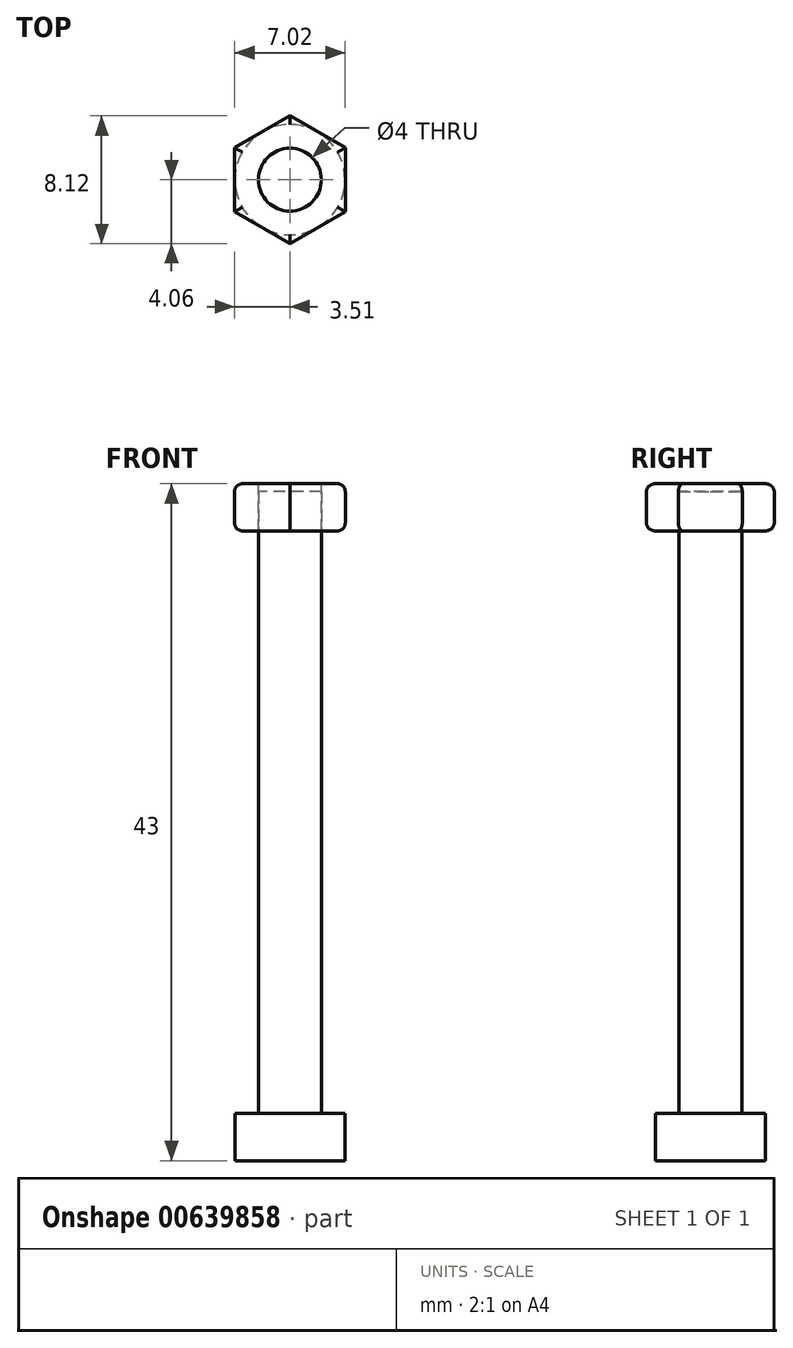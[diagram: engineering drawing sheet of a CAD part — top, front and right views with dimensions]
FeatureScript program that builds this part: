
annotation { "Feature Type Name" : "Feature", "Feature Type Description" : "" }
export const myFeature = defineFeature(function(context is Context, id is Id, definition is map)
    precondition{}
    {
        {
            var Q0;
            Q0=qCreatedBy(makeId("Top.planeOp"),FACE);
            var sketch = newSketch(context, id + "F0", { "sketchPlane" : qUnion([Q0])});
            skCircle(sketch, "E0", {"center": v(0, 0) * mm, "radius": 2 * mm});
            skCircle(sketch, "E1", {"center": v(0, 0) * mm, "radius": 3.5 * mm});
            skSolve(sketch);
        }
        {
            var Q0;
            Q0=makeQuery(id+"F0.imprint","IMPRINT",FACE,{"disambiguationData":[TD([[makeQuery(id+"F0.imprint","IMPRINT",EDGE,{"derivedFrom":sQuery(id+"F0.wireOp",EDGE,"E0")}),1.0]])]});
            extrude(context, id + "F1", {"entities" : qUnion([Q0]), "depth" : 40 * mm, "offsetDistance" : 25 * mm});
        }
        {
            var Q0;
            Q0=makeQuery(id+"F0.imprint","IMPRINT",FACE,{"disambiguationData":[TD([[makeQuery(id+"F0.imprint","IMPRINT",EDGE,{"derivedFrom":sQuery(id+"F0.wireOp",EDGE,"E0")}),-1.0]])]});
            var Q1;
            Q1=makeQuery(id+"F0.imprint","IMPRINT",FACE,{"disambiguationData":[TD([[makeQuery(id+"F0.imprint","IMPRINT",EDGE,{"derivedFrom":sQuery(id+"F0.wireOp",EDGE,"E0")}),1.0]])]});
            extrude(context, id + "F2", {"entities" : qUnion([Q0, Q1]), "operationType" : NewBodyOperationType.ADD, "oppositeDirection" : true, "depth" : 3 * mm, "offsetDistance" : 25 * mm});
        }
        {
            var Q0;
            Q0=makeQuery(id+"F1.opExtrude","CAP_FACE",FACE,{"disambiguationData":[OSD([sQuery(id+"F0.wireOp",EDGE,"E0")])],"isStart":false});
            var sketch = newSketch(context, id + "F3", { "sketchPlane" : qUnion([Q0])});
            skCircle(sketch, "E2.cCircle", {"center": v(0, 0) * mm, "radius": 3.51 * mm, "construction": true});
            skLineSegment(sketch, "E2.0", {"start": v(3.51, 2.03) * mm, "end": v(3.51, -2.03) * mm});
            skLineSegment(sketch, "E2.1", {"start": v(3.51, -2.03) * mm, "end": v(0, -4.06) * mm});
            skLineSegment(sketch, "E2.2", {"start": v(0, -4.06) * mm, "end": v(-3.51, -2.03) * mm});
            skLineSegment(sketch, "E2.3", {"start": v(-3.51, -2.03) * mm, "end": v(-3.51, 2.03) * mm});
            skLineSegment(sketch, "E2.4", {"start": v(-3.51, 2.03) * mm, "end": v(0, 4.06) * mm});
            skLineSegment(sketch, "E2.5", {"start": v(0, 4.06) * mm, "end": v(3.51, 2.03) * mm});
            skPoint(sketch, "E2.0.midPoint", {"position": v(3.51, 0) * mm});
            skCircle(sketch, "E3.0", {"center": v(0, 0) * mm, "radius": 2 * mm});
            skSolve(sketch);
        }
        {
            var Q0;
            Q0=makeQuery(id+"F3.imprint","IMPRINT",FACE,{"disambiguationData":[TD([[makeQuery(id+"F3.imprint","IMPRINT",EDGE,{"derivedFrom":sQuery(id+"F3.wireOp",EDGE,"E2.0")}),-1.0]])]});
            extrude(context, id + "F4", {"entities" : qUnion([Q0]), "oppositeDirection" : true, "depth" : 3 * mm, "offsetDistance" : 25 * mm});
        }
        {
            var Q0;
            Q0=makeQuery(id+"F3.imprint","IMPRINT",FACE,{"disambiguationData":[TD([[makeQuery(id+"F3.imprint","IMPRINT",EDGE,{"derivedFrom":sQuery(id+"F3.wireOp",EDGE,"E3.0")}),1.0]])]});
            extrude(context, id + "F5", {"entities" : qUnion([Q0]), "operationType" : NewBodyOperationType.REMOVE, "oppositeDirection" : true, "depth" : .5 * mm, "offsetDistance" : 25 * mm});
        }
        {
            var Q0;
            Q0=makeQuery(id+"F4.opExtrude","CAP_EDGE",EDGE,{"disambiguationData":[OSD([sQuery(id+"F3.wireOp",EDGE,"E2.0")])],"isStart":true});
            var Q1;
            Q1=makeQuery(id+"F4.opExtrude","CAP_EDGE",EDGE,{"disambiguationData":[OSD([sQuery(id+"F3.wireOp",EDGE,"E2.5")])],"isStart":true});
            var Q2;
            Q2=makeQuery(id+"F4.opExtrude","CAP_EDGE",EDGE,{"disambiguationData":[OSD([sQuery(id+"F3.wireOp",EDGE,"E2.4")])],"isStart":true});
            var Q3;
            Q3=makeQuery(id+"F4.opExtrude","CAP_EDGE",EDGE,{"disambiguationData":[OSD([sQuery(id+"F3.wireOp",EDGE,"E2.3")])],"isStart":true});
            var Q4;
            Q4=makeQuery(id+"F4.opExtrude","CAP_EDGE",EDGE,{"disambiguationData":[OSD([sQuery(id+"F3.wireOp",EDGE,"E2.2")])],"isStart":true});
            var Q5;
            Q5=makeQuery(id+"F4.opExtrude","CAP_EDGE",EDGE,{"disambiguationData":[OSD([sQuery(id+"F3.wireOp",EDGE,"E2.1")])],"isStart":true});
            var Q6;
            Q6=makeQuery(id+"F4.opExtrude","CAP_EDGE",EDGE,{"disambiguationData":[OSD([sQuery(id+"F3.wireOp",EDGE,"E2.1")])],"isStart":false});
            var Q7;
            Q7=makeQuery(id+"F4.opExtrude","CAP_EDGE",EDGE,{"disambiguationData":[OSD([sQuery(id+"F3.wireOp",EDGE,"E2.2")])],"isStart":false});
            var Q8;
            Q8=makeQuery(id+"F4.opExtrude","CAP_EDGE",EDGE,{"disambiguationData":[OSD([sQuery(id+"F3.wireOp",EDGE,"E2.3")])],"isStart":false});
            var Q9;
            Q9=makeQuery(id+"F4.opExtrude","CAP_EDGE",EDGE,{"disambiguationData":[OSD([sQuery(id+"F3.wireOp",EDGE,"E2.4")])],"isStart":false});
            var Q10;
            Q10=makeQuery(id+"F4.opExtrude","CAP_EDGE",EDGE,{"disambiguationData":[OSD([sQuery(id+"F3.wireOp",EDGE,"E2.5")])],"isStart":false});
            var Q11;
            Q11=makeQuery(id+"F4.opExtrude","CAP_EDGE",EDGE,{"disambiguationData":[OSD([sQuery(id+"F3.wireOp",EDGE,"E2.0")])],"isStart":false});
            fillet(context, id + "F6", {"entities" : qUnion([Q0, Q1, Q2, Q3, Q4, Q5, Q6, Q7, Q8, Q9, Q10, Q11]), "radius" : .5 * mm, "tangentPropagation" : true, "allowEdgeOverflow" : false});
        }
    });
